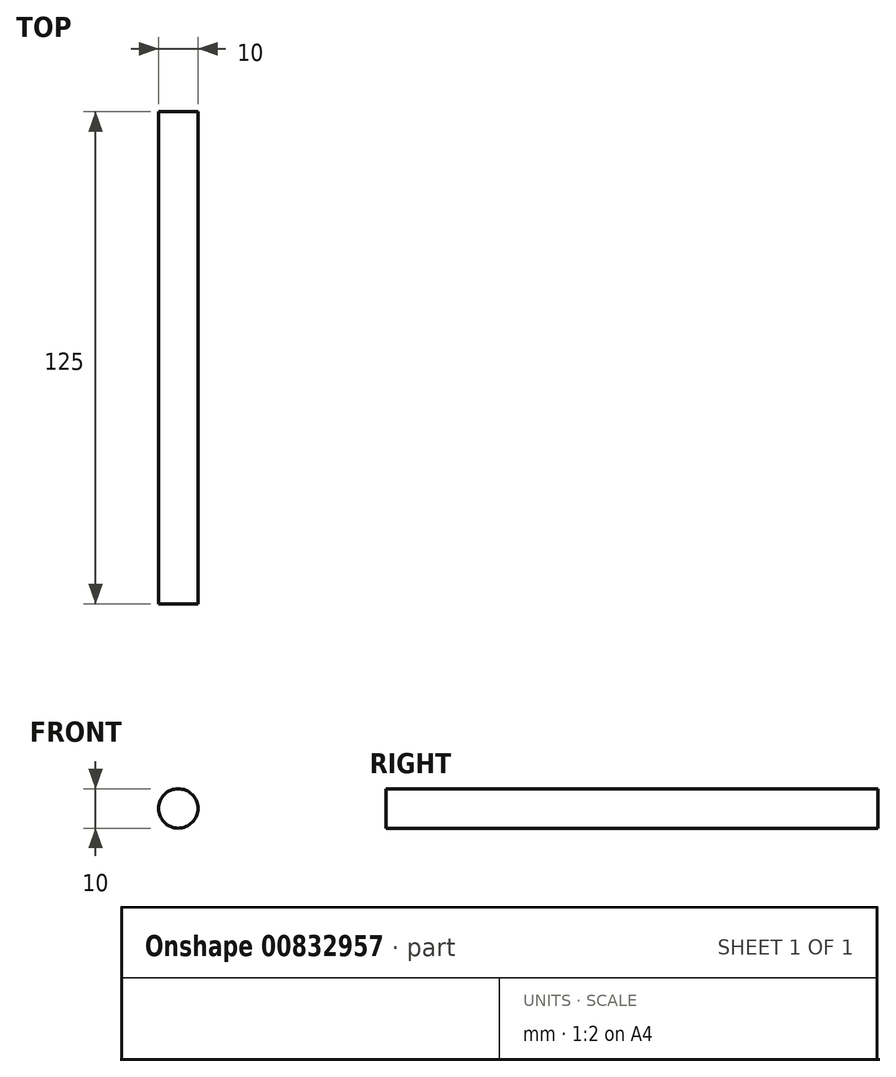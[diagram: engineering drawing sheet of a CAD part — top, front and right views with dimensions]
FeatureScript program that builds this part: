
annotation { "Feature Type Name" : "Feature", "Feature Type Description" : "" }
export const myFeature = defineFeature(function(context is Context, id is Id, definition is map)
    precondition{}
    {
        {
            var Q0;
            Q0=qCreatedBy(makeId("Front.planeOp"),FACE);
            var sketch = newSketch(context, id + "F0", { "sketchPlane" : qUnion([Q0])});
            skPoint(sketch, "E0.third.point", {"position": v(77.43, -43.66) * mm});
            skCircle(sketch, "E1", {"center": v(62.84, 12.63) * mm, "radius": 5 * mm});
            skSolve(sketch);
        }
        {
            var Q0;
            Q0=makeQuery(id+"F0.imprint","IMPRINT",FACE,{"disambiguationData":[TD([[makeQuery(id+"F0.imprint","IMPRINT",EDGE,{"derivedFrom":sQuery(id+"F0.wireOp",EDGE,"E1")}),1.0]])]});
            extrude(context, id + "F1", {"entities" : qUnion([Q0]), "depth" : 125 * mm, "offsetDistance" : 25 * mm});
        }
    });
